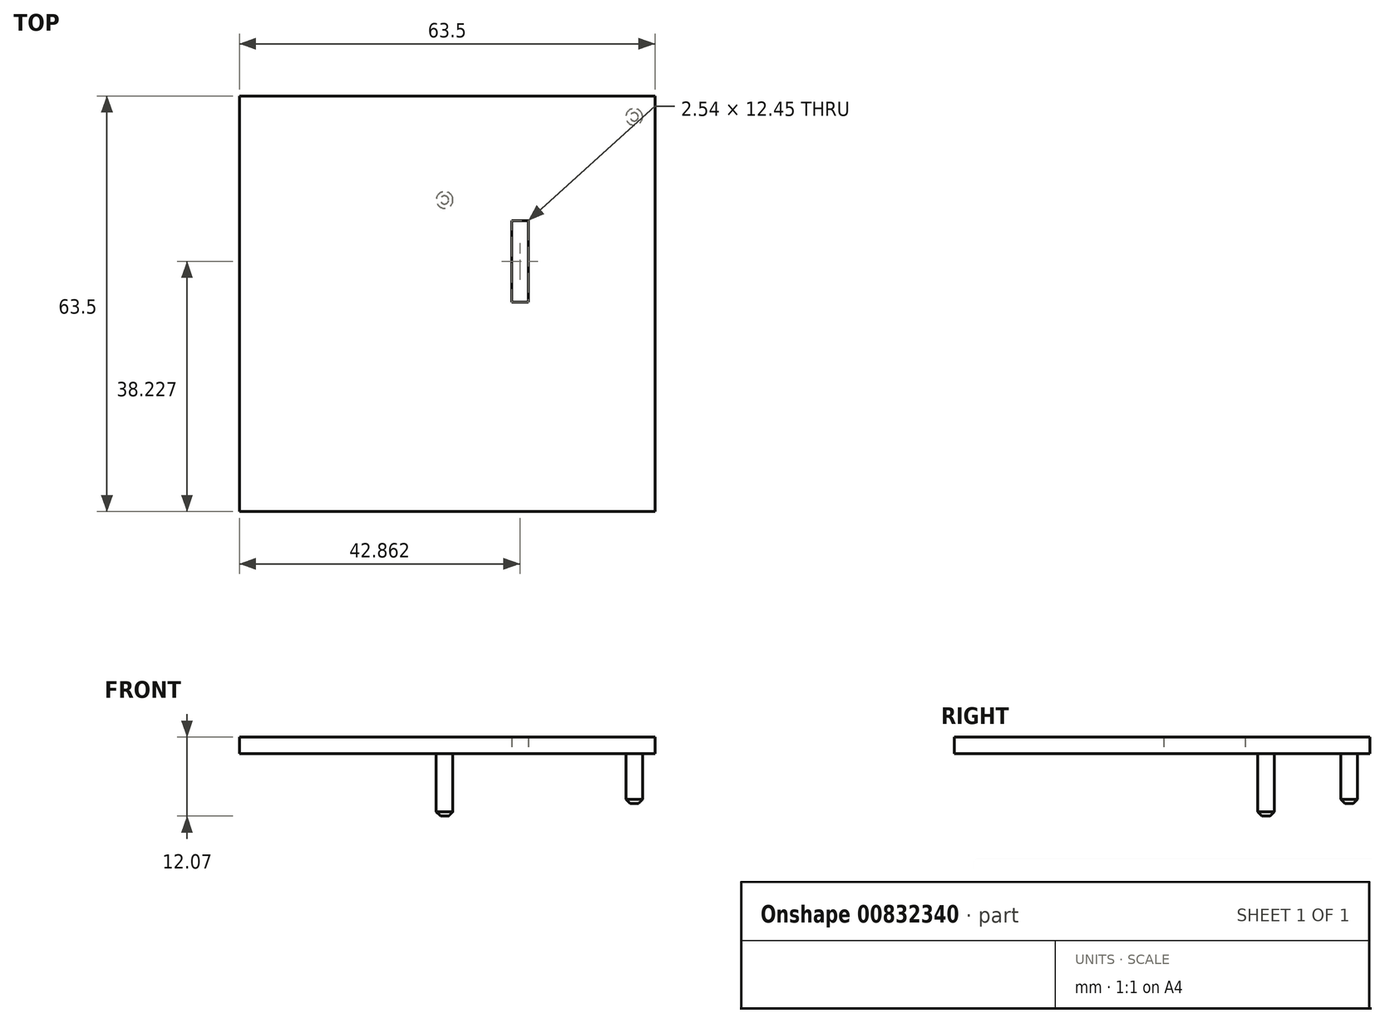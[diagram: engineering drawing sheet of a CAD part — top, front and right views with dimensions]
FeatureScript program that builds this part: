
annotation { "Feature Type Name" : "Feature", "Feature Type Description" : "" }
export const myFeature = defineFeature(function(context is Context, id is Id, definition is map)
    precondition{}
    {
        {
            var Q0;
            Q0=qCreatedBy(makeId("Top.planeOp"),FACE);
            var sketch = newSketch(context, id + "F0", { "sketchPlane" : qUnion([Q0])});
            skLineSegment(sketch, "E0.bottom", {"start": v(0, 0) * mm, "end": v(63.5, 0) * mm});
            skLineSegment(sketch, "E0.top", {"start": v(0, 63.5) * mm, "end": v(63.5, 63.5) * mm});
            skLineSegment(sketch, "E0.left", {"start": v(0, 0) * mm, "end": v(0, 63.5) * mm});
            skLineSegment(sketch, "E0.right", {"start": v(63.5, 0) * mm, "end": v(63.5, 63.5) * mm});
            skLineSegment(sketch, "E1.bottom", {"start": v(41.6, 44.45) * mm, "end": v(44.13, 44.45) * mm});
            skLineSegment(sketch, "E1.top", {"start": v(41.6, 32) * mm, "end": v(44.13, 32) * mm});
            skLineSegment(sketch, "E1.left", {"start": v(41.6, 44.45) * mm, "end": v(41.6, 32) * mm});
            skLineSegment(sketch, "E1.right", {"start": v(44.13, 44.45) * mm, "end": v(44.13, 32) * mm});
            skCircle(sketch, "E2", {"center": v(60.32, 60.32) * mm, "radius": 1.27 * mm});
            skCircle(sketch, "E3", {"center": v(31.35, 47.62) * mm, "radius": 1.27 * mm});
            skPoint(sketch, "E4", {"position": v(42.86, 44.45) * mm});
            skSolve(sketch);
        }
        {
            var Q0;
            Q0 = qSketchRegion(id + "F0", true);
            extrude(context, id + "F1", {"entities" : qUnion([Q0]), "depth" : 2.54 * mm, "offsetDistance" : 25.4 * mm});
        }
        {
            var Q0;
            Q0=qCreatedBy(makeId("Top.planeOp"),FACE);
            var sketch = newSketch(context, id + "F2", { "sketchPlane" : qUnion([Q0])});
            skCircle(sketch, "E5.0", {"center": v(31.35, 47.62) * mm, "radius": 1.27 * mm});
            skCircle(sketch, "E5.1", {"center": v(60.32, 60.32) * mm, "radius": 1.27 * mm});
            skSolve(sketch);
        }
        {
            var Q0;
            Q0 = qSketchRegion(id + "F2", true);
            extrude(context, id + "F3", {"entities" : qUnion([Q0]), "operationType" : NewBodyOperationType.ADD, "depth" : 2.54 * mm, "offsetDistance" : 25.4 * mm, "hasSecondDirection" : true, "secondDirectionOppositeDirection" : true, "secondDirectionDepth" : 7.62 * mm});
        }
        {
            var Q0;
            Q0=makeQuery(id+"F2.imprint","IMPRINT",FACE,{"disambiguationData":[TD([[makeQuery(id+"F2.imprint","IMPRINT",EDGE,{"derivedFrom":sQuery(id+"F2.wireOp",EDGE,"E5.0")}),1.0]])]});
            extrude(context, id + "F4", {"entities" : qUnion([Q0]), "operationType" : NewBodyOperationType.ADD, "oppositeDirection" : true, "depth" : 9.52 * mm, "offsetDistance" : 25.4 * mm});
        }
        {
            var Q0;
            Q0=makeQuery(id+"F3.opExtrude","CAP_EDGE",EDGE,{"disambiguationData":[OSD([sQuery(id+"F2.wireOp",EDGE,"E5.1")])],"isStart":true});
            var Q1;
            Q1=makeQuery(id+"F4.opExtrude","CAP_EDGE",EDGE,{"disambiguationData":[OSD([sQuery(id+"F2.wireOp",EDGE,"E5.0")])],"isStart":false});
            chamfer(context, id + "F5", {"entities" : qUnion([Q0, Q1]), "width" : 0.65 * mm, "tangentPropagation" : true});
        }
    });
